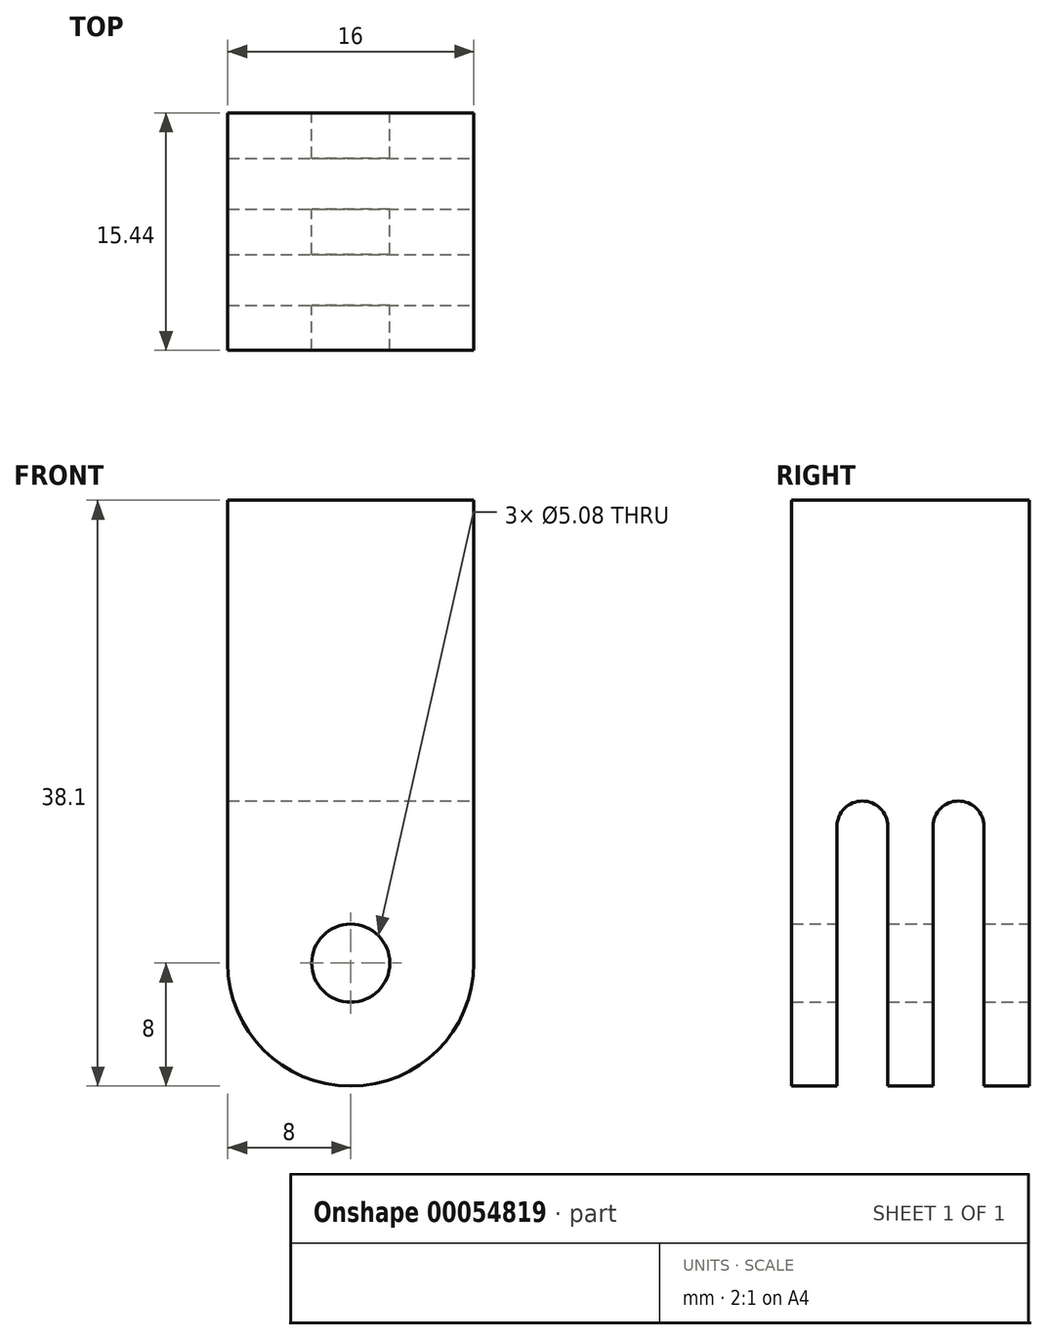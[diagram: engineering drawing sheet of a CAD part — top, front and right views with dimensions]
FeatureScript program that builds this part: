
annotation { "Feature Type Name" : "Feature", "Feature Type Description" : "" }
export const myFeature = defineFeature(function(context is Context, id is Id, definition is map)
    precondition{}
    {
        {
            var Q0;
            Q0=qCreatedBy(makeId("Front.planeOp"),FACE);
            var sketch = newSketch(context, id + "F0", { "sketchPlane" : qUnion([Q0])});
            skArc(sketch, "E0", {"start": v(-8, 0) * mm, "mid": v(0, -8) * mm, "end": v(8, 0) * mm});
            skLineSegment(sketch, "E1", {"start": v(-8, 0) * mm, "end": v(-8, 30.1) * mm});
            skLineSegment(sketch, "E2", {"start": v(-8, 30.1) * mm, "end": v(8, 30.1) * mm});
            skLineSegment(sketch, "E3", {"start": v(8, 30.1) * mm, "end": v(8, 0) * mm});
            skCircle(sketch, "E4", {"center": v(0, 0) * mm, "radius": 2.54 * mm});
            skSolve(sketch);
        }
        {
            var Q0;
            Q0 = qSketchRegion(id + "F0", true);
            extrude(context, id + "F1", {"entities" : qUnion([Q0]), "depth" : 7.72 * mm, "hasSecondDirection" : true, "secondDirectionOppositeDirection" : true, "secondDirectionDepth" : 7.72 * mm});
        }
        {
            var Q0;
            Q0=qCreatedBy(makeId("Right.planeOp"),FACE);
            var sketch = newSketch(context, id + "F2", { "sketchPlane" : qUnion([Q0])});
            skLineSegment(sketch, "E5.top", {"start": v(1.47, -10.75) * mm, "end": v(4.78, -10.75) * mm});
            skLineSegment(sketch, "E5.left", {"start": v(1.47, 8.9) * mm, "end": v(1.47, -10.75) * mm});
            skLineSegment(sketch, "E5.right", {"start": v(4.78, 8.9) * mm, "end": v(4.78, -10.75) * mm});
            skLineSegment(sketch, "E6.top", {"start": v(-4.78, -10.75) * mm, "end": v(-1.47, -10.75) * mm});
            skLineSegment(sketch, "E6.left", {"start": v(-4.78, 8.9) * mm, "end": v(-4.78, -10.75) * mm});
            skLineSegment(sketch, "E6.right", {"start": v(-1.47, 8.9) * mm, "end": v(-1.47, -10.75) * mm});
            skArc(sketch, "E7", {"start": v(-1.47, 8.9) * mm, "mid": v(-3.12, 10.54) * mm, "end": v(-4.78, 8.9) * mm});
            skPoint(sketch, "E7.first.point", {"position": v(-4.78, 8.9) * mm});
            skPoint(sketch, "E7.third.point", {"position": v(-1.47, 8.9) * mm});
            skArc(sketch, "E8", {"start": v(4.78, 8.9) * mm, "mid": v(3.12, 10.54) * mm, "end": v(1.47, 8.9) * mm});
            skPoint(sketch, "E8.first.point", {"position": v(1.47, 8.9) * mm});
            skPoint(sketch, "E8.third.point", {"position": v(4.78, 8.9) * mm});
            skSolve(sketch);
        }
        {
            var Q0;
            Q0 = qSketchRegion(id + "F2", true);
            extrude(context, id + "F3", {"entities" : qUnion([Q0]), "operationType" : NewBodyOperationType.REMOVE, "endBound" : BoundingType.THROUGH_ALL, "oppositeDirection" : true, "depth" : 25.4 * mm, "hasSecondDirection" : true, "secondDirectionBound" : BoundingType.THROUGH_ALL, "secondDirectionOppositeDirection" : false, "secondDirectionDepth" : 25.4 * mm});
        }
    });
